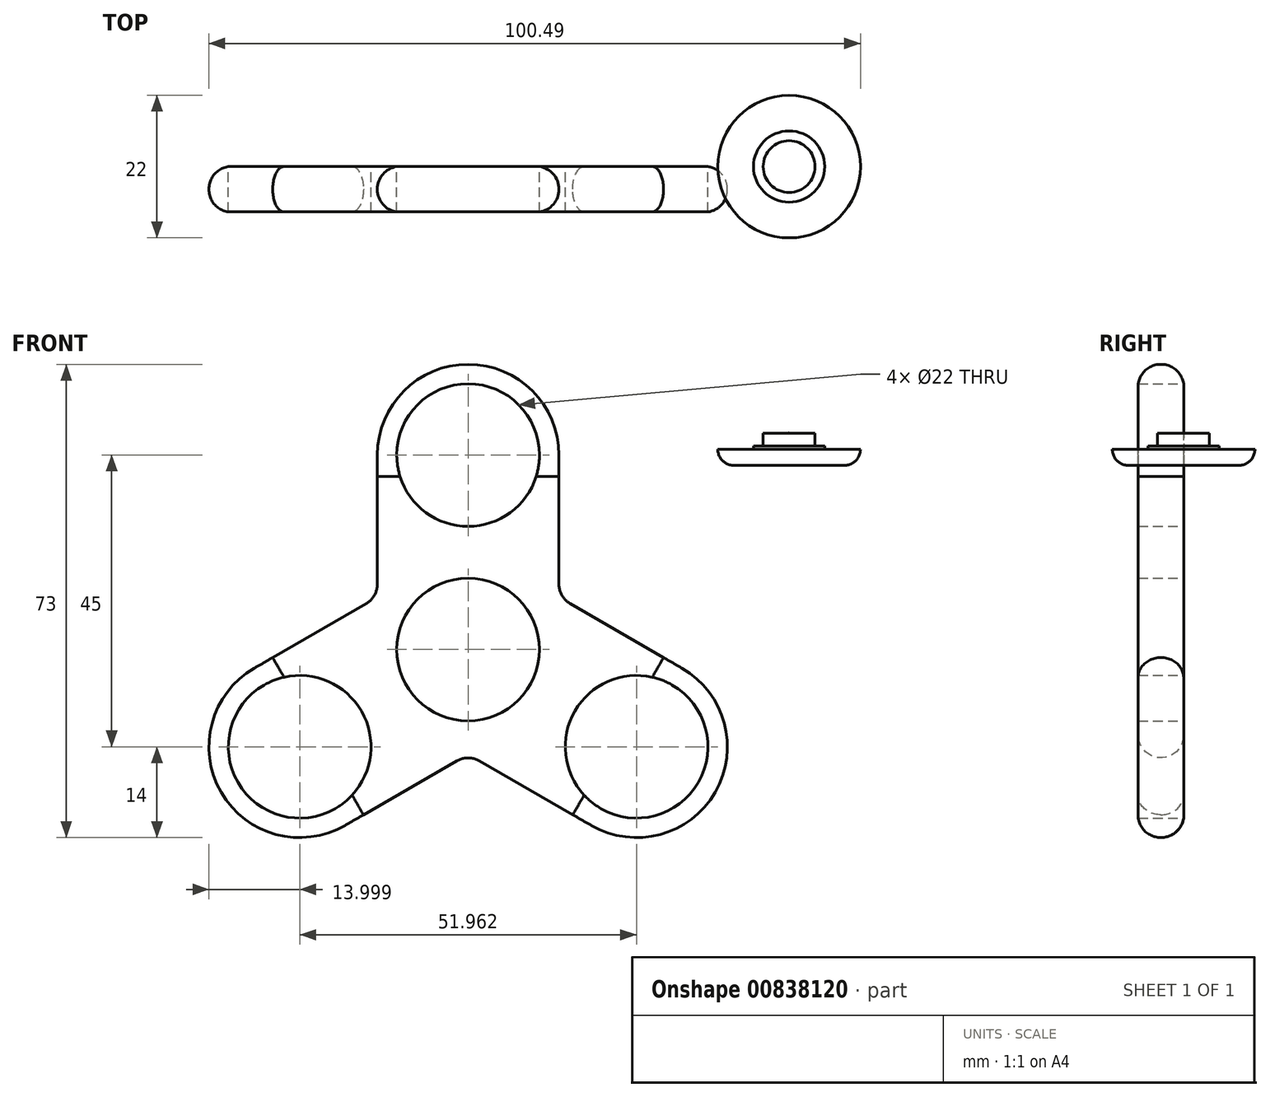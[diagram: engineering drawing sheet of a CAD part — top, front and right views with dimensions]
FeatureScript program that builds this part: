
annotation { "Feature Type Name" : "Feature", "Feature Type Description" : "" }
export const myFeature = defineFeature(function(context is Context, id is Id, definition is map)
    precondition{}
    {
        {
            var Q0;
            Q0=qCreatedBy(makeId("Front.planeOp"),FACE);
            var sketch = newSketch(context, id + "F0", { "sketchPlane" : qUnion([Q0])});
            skArc(sketch, "E0", {"start": v(14, 30) * mm, "mid": v(0, 44) * mm, "end": v(-14, 30) * mm});
            skCircle(sketch, "E1", {"center": v(0, 30) * mm, "radius": 11 * mm});
            skLineSegment(sketch, "E2", {"start": v(-14, 30) * mm, "end": v(-14, 8.08) * mm});
            skLineSegment(sketch, "E3", {"start": v(14, 30) * mm, "end": v(14, 8.08) * mm});
            skLineSegment(sketch, "E4.1.0", {"start": v(-18.98, -27.12) * mm, "end": v(0, -16.17) * mm});
            skCircle(sketch, "E4.1.2", {"center": v(-25.98, -15) * mm, "radius": 11 * mm});
            skArc(sketch, "E4.1.4", {"start": v(-32.98, -2.88) * mm, "mid": v(-38.1, -22) * mm, "end": v(-18.98, -27.12) * mm});
            skLineSegment(sketch, "E4.1.5", {"start": v(-32.98, -2.88) * mm, "end": v(-14, 8.08) * mm});
            skLineSegment(sketch, "E4.2.0", {"start": v(32.98, -2.88) * mm, "end": v(14, 8.08) * mm});
            skCircle(sketch, "E4.2.2", {"center": v(25.98, -15) * mm, "radius": 11 * mm});
            skCircle(sketch, "E4.2.3", {"center": v(0, 0) * mm, "radius": 11 * mm});
            skArc(sketch, "E4.2.4", {"start": v(18.98, -27.12) * mm, "mid": v(38.1, -22) * mm, "end": v(32.98, -2.88) * mm});
            skLineSegment(sketch, "E4.2.5", {"start": v(18.98, -27.12) * mm, "end": v(0, -16.17) * mm});
            skPoint(sketch, "E4.center", {"position": v(0, 0) * mm});
            skSolve(sketch);
        }
        {
            var Q0;
            Q0=makeQuery(id+"F0.imprint","IMPRINT",FACE,{"disambiguationData":[TD([[makeQuery(id+"F0.imprint","IMPRINT",EDGE,{"derivedFrom":sQuery(id+"F0.wireOp",EDGE,"E0")}),1.0]])]});
            extrude(context, id + "F1", {"entities" : qUnion([Q0]), "depth" : 7 * mm, "offsetDistance" : 25 * mm});
        }
        {
            var Q0;
            Q0=makeQuery(id+"F1.opExtrude","SWEPT_FACE",FACE,{"disambiguationData":[OSD([sQuery(id+"F0.wireOp",EDGE,"E0")])]});
            var Q1;
            Q1=makeQuery(id+"F1.opExtrude","SWEPT_FACE",FACE,{"disambiguationData":[OSD([sQuery(id+"F0.wireOp",EDGE,"E4.2.0")])]});
            var Q2;
            Q2=makeQuery(id+"F1.opExtrude","SWEPT_FACE",FACE,{"disambiguationData":[OSD([sQuery(id+"F0.wireOp",EDGE,"E4.2.4")])]});
            var Q3;
            Q3=makeQuery(id+"F1.opExtrude","SWEPT_FACE",FACE,{"disambiguationData":[OSD([sQuery(id+"F0.wireOp",EDGE,"E2")])]});
            var Q4;
            Q4=makeQuery(id+"F1.opExtrude","SWEPT_FACE",FACE,{"disambiguationData":[OSD([sQuery(id+"F0.wireOp",EDGE,"E4.1.5")])]});
            var Q5;
            Q5=makeQuery(id+"F1.opExtrude","SWEPT_FACE",FACE,{"disambiguationData":[OSD([sQuery(id+"F0.wireOp",EDGE,"E4.1.4")])]});
            var Q6;
            Q6=makeQuery(id+"F1.opExtrude","SWEPT_FACE",FACE,{"disambiguationData":[OSD([sQuery(id+"F0.wireOp",EDGE,"E4.1.0")])]});
            var Q7;
            Q7=makeQuery(id+"F1.opExtrude","SWEPT_FACE",FACE,{"disambiguationData":[OSD([sQuery(id+"F0.wireOp",EDGE,"E4.2.5")])]});
            fillet(context, id + "F2", {"entities" : qUnion([Q0, Q1, Q2, Q3, Q4, Q5, Q6, Q7]), "radius" : 3.5 * mm, "tangentPropagation" : true, "allowEdgeOverflow" : false});
        }
        {
            var Q0;
            Q0=qCreatedBy(makeId("Front.planeOp"),FACE);
            var sketch = newSketch(context, id + "F3", { "sketchPlane" : qUnion([Q0])});
            skLineSegment(sketch, "E5", {"start": v(49.5, 33.4) * mm, "end": v(49.5, 28.4) * mm});
            skLineSegment(sketch, "E6", {"start": v(49.5, 28.4) * mm, "end": v(60.5, 28.4) * mm});
            skLineSegment(sketch, "E7", {"start": v(60.5, 28.4) * mm, "end": v(60.5, 30.9) * mm});
            skLineSegment(sketch, "E8", {"start": v(60.5, 30.9) * mm, "end": v(55, 30.9) * mm});
            skLineSegment(sketch, "E9", {"start": v(55, 30.9) * mm, "end": v(55, 31.4) * mm});
            skLineSegment(sketch, "E10", {"start": v(55, 31.4) * mm, "end": v(53.5, 31.4) * mm});
            skLineSegment(sketch, "E11", {"start": v(53.5, 31.4) * mm, "end": v(53.5, 33.35) * mm});
            skLineSegment(sketch, "E12", {"start": v(53.5, 33.35) * mm, "end": v(49.5, 33.4) * mm});
            skSolve(sketch);
        }
        {
            var Q0;
            Q0=makeQuery(id+"F3.imprint","IMPRINT",FACE,{"disambiguationData":[TD([[makeQuery(id+"F3.imprint","IMPRINT",EDGE,{"derivedFrom":sQuery(id+"F3.wireOp",EDGE,"E5")}),1.0]])]});
            var Q1;
            Q1=sQuery(id+"F3.wireOp",EDGE,"E5");
            revolve(context, id + "F4", {"surfaceOperationType" : NewSurfaceOperationType.NEW, "entities" : qUnion([Q0]), "axis" : qUnion([Q1]), "revolveType" : RevolveType.FULL});
        }
        {
            var Q0;
            Q0=makeQuery(id+"F4.opRevolve","SWEPT_FACE",FACE,{"disambiguationData":[OSD([sQuery(id+"F3.wireOp",EDGE,"E6")])]});
            fillet(context, id + "F5", {"entities" : qUnion([Q0]), "radius" : 2.5 * mm, "tangentPropagation" : true, "allowEdgeOverflow" : false});
        }
    });
